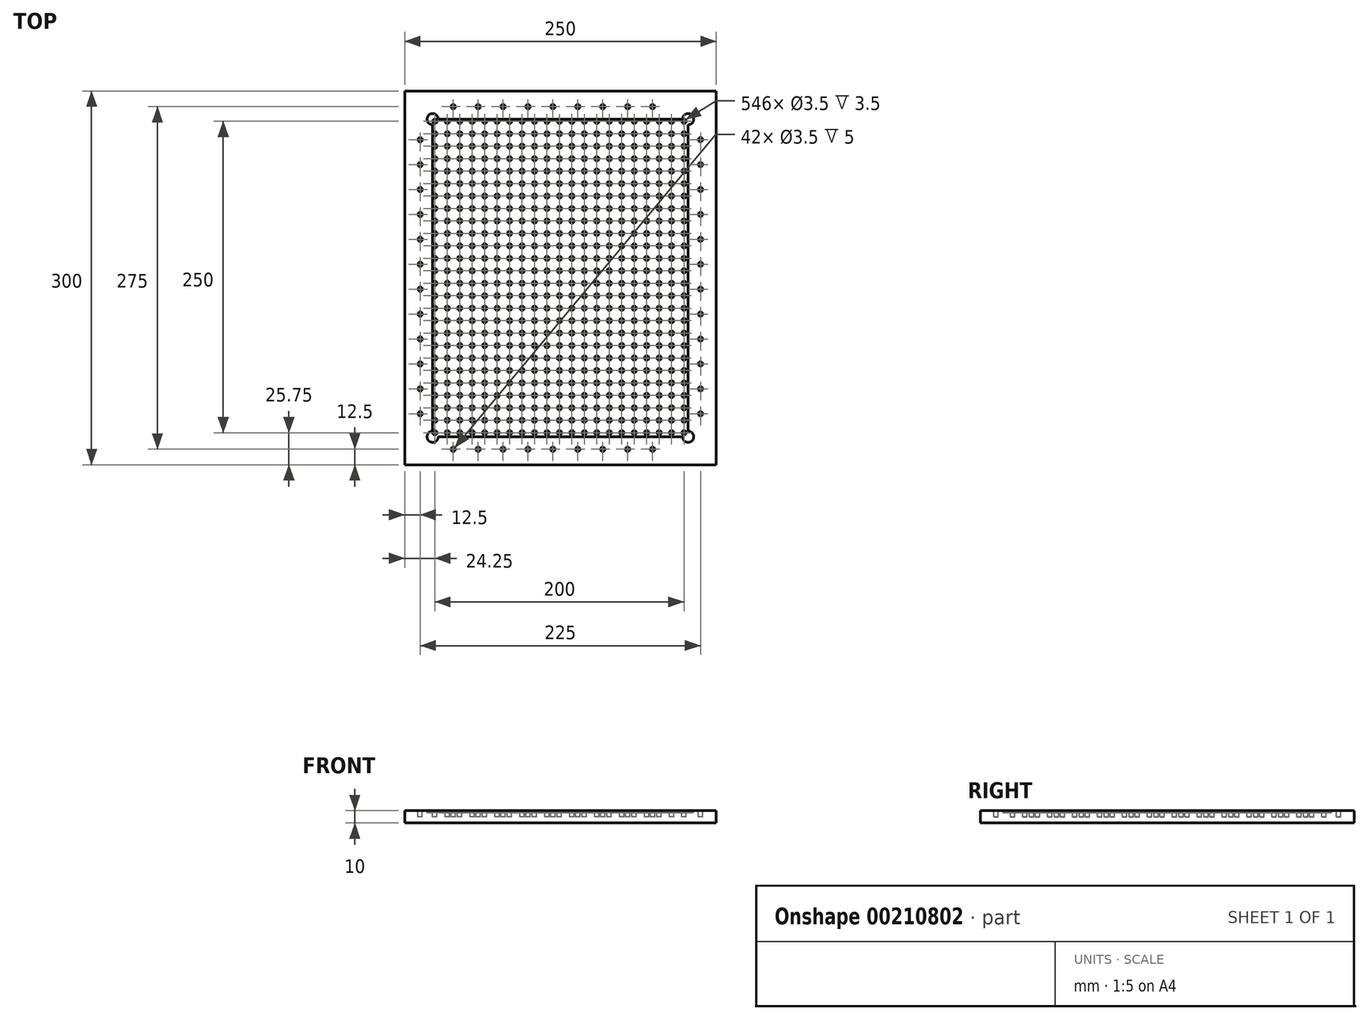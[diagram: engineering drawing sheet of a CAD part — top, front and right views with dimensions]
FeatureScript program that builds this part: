
annotation { "Feature Type Name" : "Feature", "Feature Type Description" : "" }
export const myFeature = defineFeature(function(context is Context, id is Id, definition is map)
    precondition{}
    {
        {
            var Q0;
            Q0=qCreatedBy(makeId("Top.planeOp"),FACE);
            var sketch = newSketch(context, id + "F0", { "sketchPlane" : qUnion([Q0])});
            skLineSegment(sketch, "E0.bottom", {"start": v(0, 0) * mm, "end": v(250, 0) * mm});
            skLineSegment(sketch, "E0.top", {"start": v(0, 300) * mm, "end": v(250, 300) * mm});
            skLineSegment(sketch, "E0.left", {"start": v(0, 0) * mm, "end": v(0, 300) * mm});
            skLineSegment(sketch, "E0.right", {"start": v(250, 0) * mm, "end": v(250, 300) * mm});
            skSolve(sketch);
        }
        {
            var Q0;
            Q0 = qSketchRegion(id + "F0", true);
            extrude(context, id + "F1", {"entities" : qUnion([Q0]), "depth" : 10 * mm});
        }
        {
            var Q0;
            Q0=makeQuery(id+"F1.opExtrude","CAP_FACE",FACE,{"disambiguationData":[OSD([sQuery(id+"F0.wireOp",EDGE,"E0.bottom"),sQuery(id+"F0.wireOp",EDGE,"E0.top"),sQuery(id+"F0.wireOp",EDGE,"E0.left"),sQuery(id+"F0.wireOp",EDGE,"E0.right")])],"isStart":false});
            var sketch = newSketch(context, id + "F2", { "sketchPlane" : qUnion([Q0])});
            skLineSegment(sketch, "E1.0", {"start": v(22.5, 277.5) * mm, "end": v(227.5, 277.5) * mm});
            skLineSegment(sketch, "E1.1", {"start": v(22.5, 22.5) * mm, "end": v(22.5, 277.5) * mm});
            skLineSegment(sketch, "E1.2", {"start": v(22.5, 22.5) * mm, "end": v(227.5, 22.5) * mm});
            skLineSegment(sketch, "E1.3", {"start": v(227.5, 22.5) * mm, "end": v(227.5, 277.5) * mm});
            skCircle(sketch, "E2", {"center": v(22.5, 277.5) * mm, "radius": 4.5 * mm});
            skCircle(sketch, "E3.0.1.0", {"center": v(22.5, 22.5) * mm, "radius": 4.5 * mm});
            skCircle(sketch, "E3.1.0.0", {"center": v(227.5, 277.5) * mm, "radius": 4.5 * mm});
            skCircle(sketch, "E3.1.1.0", {"center": v(227.5, 22.5) * mm, "radius": 4.5 * mm});
            skLineSegment(sketch, "E3.direction1", {"start": v(22.5, 277.5) * mm, "end": v(227.5, 277.5) * mm, "construction": true});
            skLineSegment(sketch, "E3.direction2", {"start": v(22.5, 277.5) * mm, "end": v(22.5, 22.5) * mm, "construction": true});
            skSolve(sketch);
        }
        {
            var Q0;
            Q0=makeQuery(id+"F2.imprint","IMPRINT",FACE,{"disambiguationData":[TD([[makeQuery(id+"F2.imprint","IMPRINT",EDGE,{"derivedFrom":makeQuery(id+"F1.opExtrude","CAP_EDGE",EDGE,{"disambiguationData":[OSD([sQuery(id+"F0.wireOp",EDGE,"E0.bottom")])],"isStart":false})}),1.0]])]});
            var sketch = newSketch(context, id + "F3", { "sketchPlane" : qUnion([Q0])});
            skCircle(sketch, "E4", {"center": v(24.25, 275.75) * mm, "radius": 1.75 * mm});
            skCircle(sketch, "E5.0.1.0", {"center": v(24.25, 265.75) * mm, "radius": 1.75 * mm});
            skCircle(sketch, "E5.0.2.0", {"center": v(24.25, 255.75) * mm, "radius": 1.75 * mm});
            skCircle(sketch, "E5.0.3.0", {"center": v(24.25, 245.75) * mm, "radius": 1.75 * mm});
            skCircle(sketch, "E5.0.4.0", {"center": v(24.25, 235.75) * mm, "radius": 1.75 * mm});
            skCircle(sketch, "E5.0.5.0", {"center": v(24.25, 225.75) * mm, "radius": 1.75 * mm});
            skCircle(sketch, "E5.0.6.0", {"center": v(24.25, 215.75) * mm, "radius": 1.75 * mm});
            skCircle(sketch, "E5.0.7.0", {"center": v(24.25, 205.75) * mm, "radius": 1.75 * mm});
            skCircle(sketch, "E5.0.8.0", {"center": v(24.25, 195.75) * mm, "radius": 1.75 * mm});
            skCircle(sketch, "E5.0.9.0", {"center": v(24.25, 185.75) * mm, "radius": 1.75 * mm});
            skCircle(sketch, "E5.0.10.0", {"center": v(24.25, 175.75) * mm, "radius": 1.75 * mm});
            skCircle(sketch, "E5.0.11.0", {"center": v(24.25, 165.75) * mm, "radius": 1.75 * mm});
            skCircle(sketch, "E5.0.12.0", {"center": v(24.25, 155.75) * mm, "radius": 1.75 * mm});
            skCircle(sketch, "E5.0.13.0", {"center": v(24.25, 145.75) * mm, "radius": 1.75 * mm});
            skCircle(sketch, "E5.0.14.0", {"center": v(24.25, 135.75) * mm, "radius": 1.75 * mm});
            skCircle(sketch, "E5.0.15.0", {"center": v(24.25, 125.75) * mm, "radius": 1.75 * mm});
            skCircle(sketch, "E5.0.16.0", {"center": v(24.25, 115.75) * mm, "radius": 1.75 * mm});
            skCircle(sketch, "E5.0.17.0", {"center": v(24.25, 105.75) * mm, "radius": 1.75 * mm});
            skCircle(sketch, "E5.0.18.0", {"center": v(24.25, 95.75) * mm, "radius": 1.75 * mm});
            skCircle(sketch, "E5.0.19.0", {"center": v(24.25, 85.75) * mm, "radius": 1.75 * mm});
            skCircle(sketch, "E5.0.20.0", {"center": v(24.25, 75.75) * mm, "radius": 1.75 * mm});
            skCircle(sketch, "E5.0.21.0", {"center": v(24.25, 65.75) * mm, "radius": 1.75 * mm});
            skCircle(sketch, "E5.0.22.0", {"center": v(24.25, 55.75) * mm, "radius": 1.75 * mm});
            skCircle(sketch, "E5.0.23.0", {"center": v(24.25, 45.75) * mm, "radius": 1.75 * mm});
            skCircle(sketch, "E5.0.24.0", {"center": v(24.25, 35.75) * mm, "radius": 1.75 * mm});
            skCircle(sketch, "E5.0.25.0", {"center": v(24.25, 25.75) * mm, "radius": 1.75 * mm});
            skCircle(sketch, "E5.1.0.0", {"center": v(34.25, 275.75) * mm, "radius": 1.75 * mm});
            skCircle(sketch, "E5.1.1.0", {"center": v(34.25, 265.75) * mm, "radius": 1.75 * mm});
            skCircle(sketch, "E5.1.2.0", {"center": v(34.25, 255.75) * mm, "radius": 1.75 * mm});
            skCircle(sketch, "E5.1.3.0", {"center": v(34.25, 245.75) * mm, "radius": 1.75 * mm});
            skCircle(sketch, "E5.1.4.0", {"center": v(34.25, 235.75) * mm, "radius": 1.75 * mm});
            skCircle(sketch, "E5.1.5.0", {"center": v(34.25, 225.75) * mm, "radius": 1.75 * mm});
            skCircle(sketch, "E5.1.6.0", {"center": v(34.25, 215.75) * mm, "radius": 1.75 * mm});
            skCircle(sketch, "E5.1.7.0", {"center": v(34.25, 205.75) * mm, "radius": 1.75 * mm});
            skCircle(sketch, "E5.1.8.0", {"center": v(34.25, 195.75) * mm, "radius": 1.75 * mm});
            skCircle(sketch, "E5.1.9.0", {"center": v(34.25, 185.75) * mm, "radius": 1.75 * mm});
            skCircle(sketch, "E5.1.10.0", {"center": v(34.25, 175.75) * mm, "radius": 1.75 * mm});
            skCircle(sketch, "E5.1.11.0", {"center": v(34.25, 165.75) * mm, "radius": 1.75 * mm});
            skCircle(sketch, "E5.1.12.0", {"center": v(34.25, 155.75) * mm, "radius": 1.75 * mm});
            skCircle(sketch, "E5.1.13.0", {"center": v(34.25, 145.75) * mm, "radius": 1.75 * mm});
            skCircle(sketch, "E5.1.14.0", {"center": v(34.25, 135.75) * mm, "radius": 1.75 * mm});
            skCircle(sketch, "E5.1.15.0", {"center": v(34.25, 125.75) * mm, "radius": 1.75 * mm});
            skCircle(sketch, "E5.1.16.0", {"center": v(34.25, 115.75) * mm, "radius": 1.75 * mm});
            skCircle(sketch, "E5.1.17.0", {"center": v(34.25, 105.75) * mm, "radius": 1.75 * mm});
            skCircle(sketch, "E5.1.18.0", {"center": v(34.25, 95.75) * mm, "radius": 1.75 * mm});
            skCircle(sketch, "E5.1.19.0", {"center": v(34.25, 85.75) * mm, "radius": 1.75 * mm});
            skCircle(sketch, "E5.1.20.0", {"center": v(34.25, 75.75) * mm, "radius": 1.75 * mm});
            skCircle(sketch, "E5.1.21.0", {"center": v(34.25, 65.75) * mm, "radius": 1.75 * mm});
            skCircle(sketch, "E5.1.22.0", {"center": v(34.25, 55.75) * mm, "radius": 1.75 * mm});
            skCircle(sketch, "E5.1.23.0", {"center": v(34.25, 45.75) * mm, "radius": 1.75 * mm});
            skCircle(sketch, "E5.1.24.0", {"center": v(34.25, 35.75) * mm, "radius": 1.75 * mm});
            skCircle(sketch, "E5.1.25.0", {"center": v(34.25, 25.75) * mm, "radius": 1.75 * mm});
            skCircle(sketch, "E5.2.0.0", {"center": v(44.25, 275.75) * mm, "radius": 1.75 * mm});
            skCircle(sketch, "E5.2.1.0", {"center": v(44.25, 265.75) * mm, "radius": 1.75 * mm});
            skCircle(sketch, "E5.2.2.0", {"center": v(44.25, 255.75) * mm, "radius": 1.75 * mm});
            skCircle(sketch, "E5.2.3.0", {"center": v(44.25, 245.75) * mm, "radius": 1.75 * mm});
            skCircle(sketch, "E5.2.4.0", {"center": v(44.25, 235.75) * mm, "radius": 1.75 * mm});
            skCircle(sketch, "E5.2.5.0", {"center": v(44.25, 225.75) * mm, "radius": 1.75 * mm});
            skCircle(sketch, "E5.2.6.0", {"center": v(44.25, 215.75) * mm, "radius": 1.75 * mm});
            skCircle(sketch, "E5.2.7.0", {"center": v(44.25, 205.75) * mm, "radius": 1.75 * mm});
            skCircle(sketch, "E5.2.8.0", {"center": v(44.25, 195.75) * mm, "radius": 1.75 * mm});
            skCircle(sketch, "E5.2.9.0", {"center": v(44.25, 185.75) * mm, "radius": 1.75 * mm});
            skCircle(sketch, "E5.2.10.0", {"center": v(44.25, 175.75) * mm, "radius": 1.75 * mm});
            skCircle(sketch, "E5.2.11.0", {"center": v(44.25, 165.75) * mm, "radius": 1.75 * mm});
            skCircle(sketch, "E5.2.12.0", {"center": v(44.25, 155.75) * mm, "radius": 1.75 * mm});
            skCircle(sketch, "E5.2.13.0", {"center": v(44.25, 145.75) * mm, "radius": 1.75 * mm});
            skCircle(sketch, "E5.2.14.0", {"center": v(44.25, 135.75) * mm, "radius": 1.75 * mm});
            skCircle(sketch, "E5.2.15.0", {"center": v(44.25, 125.75) * mm, "radius": 1.75 * mm});
            skCircle(sketch, "E5.2.16.0", {"center": v(44.25, 115.75) * mm, "radius": 1.75 * mm});
            skCircle(sketch, "E5.2.17.0", {"center": v(44.25, 105.75) * mm, "radius": 1.75 * mm});
            skCircle(sketch, "E5.2.18.0", {"center": v(44.25, 95.75) * mm, "radius": 1.75 * mm});
            skCircle(sketch, "E5.2.19.0", {"center": v(44.25, 85.75) * mm, "radius": 1.75 * mm});
            skCircle(sketch, "E5.2.20.0", {"center": v(44.25, 75.75) * mm, "radius": 1.75 * mm});
            skCircle(sketch, "E5.2.21.0", {"center": v(44.25, 65.75) * mm, "radius": 1.75 * mm});
            skCircle(sketch, "E5.2.22.0", {"center": v(44.25, 55.75) * mm, "radius": 1.75 * mm});
            skCircle(sketch, "E5.2.23.0", {"center": v(44.25, 45.75) * mm, "radius": 1.75 * mm});
            skCircle(sketch, "E5.2.24.0", {"center": v(44.25, 35.75) * mm, "radius": 1.75 * mm});
            skCircle(sketch, "E5.2.25.0", {"center": v(44.25, 25.75) * mm, "radius": 1.75 * mm});
            skCircle(sketch, "E5.3.0.0", {"center": v(54.25, 275.75) * mm, "radius": 1.75 * mm});
            skCircle(sketch, "E5.3.1.0", {"center": v(54.25, 265.75) * mm, "radius": 1.75 * mm});
            skCircle(sketch, "E5.3.2.0", {"center": v(54.25, 255.75) * mm, "radius": 1.75 * mm});
            skCircle(sketch, "E5.3.3.0", {"center": v(54.25, 245.75) * mm, "radius": 1.75 * mm});
            skCircle(sketch, "E5.3.4.0", {"center": v(54.25, 235.75) * mm, "radius": 1.75 * mm});
            skCircle(sketch, "E5.3.5.0", {"center": v(54.25, 225.75) * mm, "radius": 1.75 * mm});
            skCircle(sketch, "E5.3.6.0", {"center": v(54.25, 215.75) * mm, "radius": 1.75 * mm});
            skCircle(sketch, "E5.3.7.0", {"center": v(54.25, 205.75) * mm, "radius": 1.75 * mm});
            skCircle(sketch, "E5.3.8.0", {"center": v(54.25, 195.75) * mm, "radius": 1.75 * mm});
            skCircle(sketch, "E5.3.9.0", {"center": v(54.25, 185.75) * mm, "radius": 1.75 * mm});
            skCircle(sketch, "E5.3.10.0", {"center": v(54.25, 175.75) * mm, "radius": 1.75 * mm});
            skCircle(sketch, "E5.3.11.0", {"center": v(54.25, 165.75) * mm, "radius": 1.75 * mm});
            skCircle(sketch, "E5.3.12.0", {"center": v(54.25, 155.75) * mm, "radius": 1.75 * mm});
            skCircle(sketch, "E5.3.13.0", {"center": v(54.25, 145.75) * mm, "radius": 1.75 * mm});
            skCircle(sketch, "E5.3.14.0", {"center": v(54.25, 135.75) * mm, "radius": 1.75 * mm});
            skCircle(sketch, "E5.3.15.0", {"center": v(54.25, 125.75) * mm, "radius": 1.75 * mm});
            skCircle(sketch, "E5.3.16.0", {"center": v(54.25, 115.75) * mm, "radius": 1.75 * mm});
            skCircle(sketch, "E5.3.17.0", {"center": v(54.25, 105.75) * mm, "radius": 1.75 * mm});
            skCircle(sketch, "E5.3.18.0", {"center": v(54.25, 95.75) * mm, "radius": 1.75 * mm});
            skCircle(sketch, "E5.3.19.0", {"center": v(54.25, 85.75) * mm, "radius": 1.75 * mm});
            skCircle(sketch, "E5.3.20.0", {"center": v(54.25, 75.75) * mm, "radius": 1.75 * mm});
            skCircle(sketch, "E5.3.21.0", {"center": v(54.25, 65.75) * mm, "radius": 1.75 * mm});
            skCircle(sketch, "E5.3.22.0", {"center": v(54.25, 55.75) * mm, "radius": 1.75 * mm});
            skCircle(sketch, "E5.3.23.0", {"center": v(54.25, 45.75) * mm, "radius": 1.75 * mm});
            skCircle(sketch, "E5.3.24.0", {"center": v(54.25, 35.75) * mm, "radius": 1.75 * mm});
            skCircle(sketch, "E5.3.25.0", {"center": v(54.25, 25.75) * mm, "radius": 1.75 * mm});
            skCircle(sketch, "E5.4.0.0", {"center": v(64.25, 275.75) * mm, "radius": 1.75 * mm});
            skCircle(sketch, "E5.4.1.0", {"center": v(64.25, 265.75) * mm, "radius": 1.75 * mm});
            skCircle(sketch, "E5.4.2.0", {"center": v(64.25, 255.75) * mm, "radius": 1.75 * mm});
            skCircle(sketch, "E5.4.3.0", {"center": v(64.25, 245.75) * mm, "radius": 1.75 * mm});
            skCircle(sketch, "E5.4.4.0", {"center": v(64.25, 235.75) * mm, "radius": 1.75 * mm});
            skCircle(sketch, "E5.4.5.0", {"center": v(64.25, 225.75) * mm, "radius": 1.75 * mm});
            skCircle(sketch, "E5.4.6.0", {"center": v(64.25, 215.75) * mm, "radius": 1.75 * mm});
            skCircle(sketch, "E5.4.7.0", {"center": v(64.25, 205.75) * mm, "radius": 1.75 * mm});
            skCircle(sketch, "E5.4.8.0", {"center": v(64.25, 195.75) * mm, "radius": 1.75 * mm});
            skCircle(sketch, "E5.4.9.0", {"center": v(64.25, 185.75) * mm, "radius": 1.75 * mm});
            skCircle(sketch, "E5.4.10.0", {"center": v(64.25, 175.75) * mm, "radius": 1.75 * mm});
            skCircle(sketch, "E5.4.11.0", {"center": v(64.25, 165.75) * mm, "radius": 1.75 * mm});
            skCircle(sketch, "E5.4.12.0", {"center": v(64.25, 155.75) * mm, "radius": 1.75 * mm});
            skCircle(sketch, "E5.4.13.0", {"center": v(64.25, 145.75) * mm, "radius": 1.75 * mm});
            skCircle(sketch, "E5.4.14.0", {"center": v(64.25, 135.75) * mm, "radius": 1.75 * mm});
            skCircle(sketch, "E5.4.15.0", {"center": v(64.25, 125.75) * mm, "radius": 1.75 * mm});
            skCircle(sketch, "E5.4.16.0", {"center": v(64.25, 115.75) * mm, "radius": 1.75 * mm});
            skCircle(sketch, "E5.4.17.0", {"center": v(64.25, 105.75) * mm, "radius": 1.75 * mm});
            skCircle(sketch, "E5.4.18.0", {"center": v(64.25, 95.75) * mm, "radius": 1.75 * mm});
            skCircle(sketch, "E5.4.19.0", {"center": v(64.25, 85.75) * mm, "radius": 1.75 * mm});
            skCircle(sketch, "E5.4.20.0", {"center": v(64.25, 75.75) * mm, "radius": 1.75 * mm});
            skCircle(sketch, "E5.4.21.0", {"center": v(64.25, 65.75) * mm, "radius": 1.75 * mm});
            skCircle(sketch, "E5.4.22.0", {"center": v(64.25, 55.75) * mm, "radius": 1.75 * mm});
            skCircle(sketch, "E5.4.23.0", {"center": v(64.25, 45.75) * mm, "radius": 1.75 * mm});
            skCircle(sketch, "E5.4.24.0", {"center": v(64.25, 35.75) * mm, "radius": 1.75 * mm});
            skCircle(sketch, "E5.4.25.0", {"center": v(64.25, 25.75) * mm, "radius": 1.75 * mm});
            skCircle(sketch, "E5.5.0.0", {"center": v(74.25, 275.75) * mm, "radius": 1.75 * mm});
            skCircle(sketch, "E5.5.1.0", {"center": v(74.25, 265.75) * mm, "radius": 1.75 * mm});
            skCircle(sketch, "E5.5.2.0", {"center": v(74.25, 255.75) * mm, "radius": 1.75 * mm});
            skCircle(sketch, "E5.5.3.0", {"center": v(74.25, 245.75) * mm, "radius": 1.75 * mm});
            skCircle(sketch, "E5.5.4.0", {"center": v(74.25, 235.75) * mm, "radius": 1.75 * mm});
            skCircle(sketch, "E5.5.5.0", {"center": v(74.25, 225.75) * mm, "radius": 1.75 * mm});
            skCircle(sketch, "E5.5.6.0", {"center": v(74.25, 215.75) * mm, "radius": 1.75 * mm});
            skCircle(sketch, "E5.5.7.0", {"center": v(74.25, 205.75) * mm, "radius": 1.75 * mm});
            skCircle(sketch, "E5.5.8.0", {"center": v(74.25, 195.75) * mm, "radius": 1.75 * mm});
            skCircle(sketch, "E5.5.9.0", {"center": v(74.25, 185.75) * mm, "radius": 1.75 * mm});
            skCircle(sketch, "E5.5.10.0", {"center": v(74.25, 175.75) * mm, "radius": 1.75 * mm});
            skCircle(sketch, "E5.5.11.0", {"center": v(74.25, 165.75) * mm, "radius": 1.75 * mm});
            skCircle(sketch, "E5.5.12.0", {"center": v(74.25, 155.75) * mm, "radius": 1.75 * mm});
            skCircle(sketch, "E5.5.13.0", {"center": v(74.25, 145.75) * mm, "radius": 1.75 * mm});
            skCircle(sketch, "E5.5.14.0", {"center": v(74.25, 135.75) * mm, "radius": 1.75 * mm});
            skCircle(sketch, "E5.5.15.0", {"center": v(74.25, 125.75) * mm, "radius": 1.75 * mm});
            skCircle(sketch, "E5.5.16.0", {"center": v(74.25, 115.75) * mm, "radius": 1.75 * mm});
            skCircle(sketch, "E5.5.17.0", {"center": v(74.25, 105.75) * mm, "radius": 1.75 * mm});
            skCircle(sketch, "E5.5.18.0", {"center": v(74.25, 95.75) * mm, "radius": 1.75 * mm});
            skCircle(sketch, "E5.5.19.0", {"center": v(74.25, 85.75) * mm, "radius": 1.75 * mm});
            skCircle(sketch, "E5.5.20.0", {"center": v(74.25, 75.75) * mm, "radius": 1.75 * mm});
            skCircle(sketch, "E5.5.21.0", {"center": v(74.25, 65.75) * mm, "radius": 1.75 * mm});
            skCircle(sketch, "E5.5.22.0", {"center": v(74.25, 55.75) * mm, "radius": 1.75 * mm});
            skCircle(sketch, "E5.5.23.0", {"center": v(74.25, 45.75) * mm, "radius": 1.75 * mm});
            skCircle(sketch, "E5.5.24.0", {"center": v(74.25, 35.75) * mm, "radius": 1.75 * mm});
            skCircle(sketch, "E5.5.25.0", {"center": v(74.25, 25.75) * mm, "radius": 1.75 * mm});
            skCircle(sketch, "E5.6.0.0", {"center": v(84.25, 275.75) * mm, "radius": 1.75 * mm});
            skCircle(sketch, "E5.6.1.0", {"center": v(84.25, 265.75) * mm, "radius": 1.75 * mm});
            skCircle(sketch, "E5.6.2.0", {"center": v(84.25, 255.75) * mm, "radius": 1.75 * mm});
            skCircle(sketch, "E5.6.3.0", {"center": v(84.25, 245.75) * mm, "radius": 1.75 * mm});
            skCircle(sketch, "E5.6.4.0", {"center": v(84.25, 235.75) * mm, "radius": 1.75 * mm});
            skCircle(sketch, "E5.6.5.0", {"center": v(84.25, 225.75) * mm, "radius": 1.75 * mm});
            skCircle(sketch, "E5.6.6.0", {"center": v(84.25, 215.75) * mm, "radius": 1.75 * mm});
            skCircle(sketch, "E5.6.7.0", {"center": v(84.25, 205.75) * mm, "radius": 1.75 * mm});
            skCircle(sketch, "E5.6.8.0", {"center": v(84.25, 195.75) * mm, "radius": 1.75 * mm});
            skCircle(sketch, "E5.6.9.0", {"center": v(84.25, 185.75) * mm, "radius": 1.75 * mm});
            skCircle(sketch, "E5.6.10.0", {"center": v(84.25, 175.75) * mm, "radius": 1.75 * mm});
            skCircle(sketch, "E5.6.11.0", {"center": v(84.25, 165.75) * mm, "radius": 1.75 * mm});
            skCircle(sketch, "E5.6.12.0", {"center": v(84.25, 155.75) * mm, "radius": 1.75 * mm});
            skCircle(sketch, "E5.6.13.0", {"center": v(84.25, 145.75) * mm, "radius": 1.75 * mm});
            skCircle(sketch, "E5.6.14.0", {"center": v(84.25, 135.75) * mm, "radius": 1.75 * mm});
            skCircle(sketch, "E5.6.15.0", {"center": v(84.25, 125.75) * mm, "radius": 1.75 * mm});
            skCircle(sketch, "E5.6.16.0", {"center": v(84.25, 115.75) * mm, "radius": 1.75 * mm});
            skCircle(sketch, "E5.6.17.0", {"center": v(84.25, 105.75) * mm, "radius": 1.75 * mm});
            skCircle(sketch, "E5.6.18.0", {"center": v(84.25, 95.75) * mm, "radius": 1.75 * mm});
            skCircle(sketch, "E5.6.19.0", {"center": v(84.25, 85.75) * mm, "radius": 1.75 * mm});
            skCircle(sketch, "E5.6.20.0", {"center": v(84.25, 75.75) * mm, "radius": 1.75 * mm});
            skCircle(sketch, "E5.6.21.0", {"center": v(84.25, 65.75) * mm, "radius": 1.75 * mm});
            skCircle(sketch, "E5.6.22.0", {"center": v(84.25, 55.75) * mm, "radius": 1.75 * mm});
            skCircle(sketch, "E5.6.23.0", {"center": v(84.25, 45.75) * mm, "radius": 1.75 * mm});
            skCircle(sketch, "E5.6.24.0", {"center": v(84.25, 35.75) * mm, "radius": 1.75 * mm});
            skCircle(sketch, "E5.6.25.0", {"center": v(84.25, 25.75) * mm, "radius": 1.75 * mm});
            skCircle(sketch, "E5.7.0.0", {"center": v(94.25, 275.75) * mm, "radius": 1.75 * mm});
            skCircle(sketch, "E5.7.1.0", {"center": v(94.25, 265.75) * mm, "radius": 1.75 * mm});
            skCircle(sketch, "E5.7.2.0", {"center": v(94.25, 255.75) * mm, "radius": 1.75 * mm});
            skCircle(sketch, "E5.7.3.0", {"center": v(94.25, 245.75) * mm, "radius": 1.75 * mm});
            skCircle(sketch, "E5.7.4.0", {"center": v(94.25, 235.75) * mm, "radius": 1.75 * mm});
            skCircle(sketch, "E5.7.5.0", {"center": v(94.25, 225.75) * mm, "radius": 1.75 * mm});
            skCircle(sketch, "E5.7.6.0", {"center": v(94.25, 215.75) * mm, "radius": 1.75 * mm});
            skCircle(sketch, "E5.7.7.0", {"center": v(94.25, 205.75) * mm, "radius": 1.75 * mm});
            skCircle(sketch, "E5.7.8.0", {"center": v(94.25, 195.75) * mm, "radius": 1.75 * mm});
            skCircle(sketch, "E5.7.9.0", {"center": v(94.25, 185.75) * mm, "radius": 1.75 * mm});
            skCircle(sketch, "E5.7.10.0", {"center": v(94.25, 175.75) * mm, "radius": 1.75 * mm});
            skCircle(sketch, "E5.7.11.0", {"center": v(94.25, 165.75) * mm, "radius": 1.75 * mm});
            skCircle(sketch, "E5.7.12.0", {"center": v(94.25, 155.75) * mm, "radius": 1.75 * mm});
            skCircle(sketch, "E5.7.13.0", {"center": v(94.25, 145.75) * mm, "radius": 1.75 * mm});
            skCircle(sketch, "E5.7.14.0", {"center": v(94.25, 135.75) * mm, "radius": 1.75 * mm});
            skCircle(sketch, "E5.7.15.0", {"center": v(94.25, 125.75) * mm, "radius": 1.75 * mm});
            skCircle(sketch, "E5.7.16.0", {"center": v(94.25, 115.75) * mm, "radius": 1.75 * mm});
            skCircle(sketch, "E5.7.17.0", {"center": v(94.25, 105.75) * mm, "radius": 1.75 * mm});
            skCircle(sketch, "E5.7.18.0", {"center": v(94.25, 95.75) * mm, "radius": 1.75 * mm});
            skCircle(sketch, "E5.7.19.0", {"center": v(94.25, 85.75) * mm, "radius": 1.75 * mm});
            skCircle(sketch, "E5.7.20.0", {"center": v(94.25, 75.75) * mm, "radius": 1.75 * mm});
            skCircle(sketch, "E5.7.21.0", {"center": v(94.25, 65.75) * mm, "radius": 1.75 * mm});
            skCircle(sketch, "E5.7.22.0", {"center": v(94.25, 55.75) * mm, "radius": 1.75 * mm});
            skCircle(sketch, "E5.7.23.0", {"center": v(94.25, 45.75) * mm, "radius": 1.75 * mm});
            skCircle(sketch, "E5.7.24.0", {"center": v(94.25, 35.75) * mm, "radius": 1.75 * mm});
            skCircle(sketch, "E5.7.25.0", {"center": v(94.25, 25.75) * mm, "radius": 1.75 * mm});
            skCircle(sketch, "E5.8.0.0", {"center": v(104.25, 275.75) * mm, "radius": 1.75 * mm});
            skCircle(sketch, "E5.8.1.0", {"center": v(104.25, 265.75) * mm, "radius": 1.75 * mm});
            skCircle(sketch, "E5.8.2.0", {"center": v(104.25, 255.75) * mm, "radius": 1.75 * mm});
            skCircle(sketch, "E5.8.3.0", {"center": v(104.25, 245.75) * mm, "radius": 1.75 * mm});
            skCircle(sketch, "E5.8.4.0", {"center": v(104.25, 235.75) * mm, "radius": 1.75 * mm});
            skCircle(sketch, "E5.8.5.0", {"center": v(104.25, 225.75) * mm, "radius": 1.75 * mm});
            skCircle(sketch, "E5.8.6.0", {"center": v(104.25, 215.75) * mm, "radius": 1.75 * mm});
            skCircle(sketch, "E5.8.7.0", {"center": v(104.25, 205.75) * mm, "radius": 1.75 * mm});
            skCircle(sketch, "E5.8.8.0", {"center": v(104.25, 195.75) * mm, "radius": 1.75 * mm});
            skCircle(sketch, "E5.8.9.0", {"center": v(104.25, 185.75) * mm, "radius": 1.75 * mm});
            skCircle(sketch, "E5.8.10.0", {"center": v(104.25, 175.75) * mm, "radius": 1.75 * mm});
            skCircle(sketch, "E5.8.11.0", {"center": v(104.25, 165.75) * mm, "radius": 1.75 * mm});
            skCircle(sketch, "E5.8.12.0", {"center": v(104.25, 155.75) * mm, "radius": 1.75 * mm});
            skCircle(sketch, "E5.8.13.0", {"center": v(104.25, 145.75) * mm, "radius": 1.75 * mm});
            skCircle(sketch, "E5.8.14.0", {"center": v(104.25, 135.75) * mm, "radius": 1.75 * mm});
            skCircle(sketch, "E5.8.15.0", {"center": v(104.25, 125.75) * mm, "radius": 1.75 * mm});
            skCircle(sketch, "E5.8.16.0", {"center": v(104.25, 115.75) * mm, "radius": 1.75 * mm});
            skCircle(sketch, "E5.8.17.0", {"center": v(104.25, 105.75) * mm, "radius": 1.75 * mm});
            skCircle(sketch, "E5.8.18.0", {"center": v(104.25, 95.75) * mm, "radius": 1.75 * mm});
            skCircle(sketch, "E5.8.19.0", {"center": v(104.25, 85.75) * mm, "radius": 1.75 * mm});
            skCircle(sketch, "E5.8.20.0", {"center": v(104.25, 75.75) * mm, "radius": 1.75 * mm});
            skCircle(sketch, "E5.8.21.0", {"center": v(104.25, 65.75) * mm, "radius": 1.75 * mm});
            skCircle(sketch, "E5.8.22.0", {"center": v(104.25, 55.75) * mm, "radius": 1.75 * mm});
            skCircle(sketch, "E5.8.23.0", {"center": v(104.25, 45.75) * mm, "radius": 1.75 * mm});
            skCircle(sketch, "E5.8.24.0", {"center": v(104.25, 35.75) * mm, "radius": 1.75 * mm});
            skCircle(sketch, "E5.8.25.0", {"center": v(104.25, 25.75) * mm, "radius": 1.75 * mm});
            skCircle(sketch, "E5.9.0.0", {"center": v(114.25, 275.75) * mm, "radius": 1.75 * mm});
            skCircle(sketch, "E5.9.1.0", {"center": v(114.25, 265.75) * mm, "radius": 1.75 * mm});
            skCircle(sketch, "E5.9.2.0", {"center": v(114.25, 255.75) * mm, "radius": 1.75 * mm});
            skCircle(sketch, "E5.9.3.0", {"center": v(114.25, 245.75) * mm, "radius": 1.75 * mm});
            skCircle(sketch, "E5.9.4.0", {"center": v(114.25, 235.75) * mm, "radius": 1.75 * mm});
            skCircle(sketch, "E5.9.5.0", {"center": v(114.25, 225.75) * mm, "radius": 1.75 * mm});
            skCircle(sketch, "E5.9.6.0", {"center": v(114.25, 215.75) * mm, "radius": 1.75 * mm});
            skCircle(sketch, "E5.9.7.0", {"center": v(114.25, 205.75) * mm, "radius": 1.75 * mm});
            skCircle(sketch, "E5.9.8.0", {"center": v(114.25, 195.75) * mm, "radius": 1.75 * mm});
            skCircle(sketch, "E5.9.9.0", {"center": v(114.25, 185.75) * mm, "radius": 1.75 * mm});
            skCircle(sketch, "E5.9.10.0", {"center": v(114.25, 175.75) * mm, "radius": 1.75 * mm});
            skCircle(sketch, "E5.9.11.0", {"center": v(114.25, 165.75) * mm, "radius": 1.75 * mm});
            skCircle(sketch, "E5.9.12.0", {"center": v(114.25, 155.75) * mm, "radius": 1.75 * mm});
            skCircle(sketch, "E5.9.13.0", {"center": v(114.25, 145.75) * mm, "radius": 1.75 * mm});
            skCircle(sketch, "E5.9.14.0", {"center": v(114.25, 135.75) * mm, "radius": 1.75 * mm});
            skCircle(sketch, "E5.9.15.0", {"center": v(114.25, 125.75) * mm, "radius": 1.75 * mm});
            skCircle(sketch, "E5.9.16.0", {"center": v(114.25, 115.75) * mm, "radius": 1.75 * mm});
            skCircle(sketch, "E5.9.17.0", {"center": v(114.25, 105.75) * mm, "radius": 1.75 * mm});
            skCircle(sketch, "E5.9.18.0", {"center": v(114.25, 95.75) * mm, "radius": 1.75 * mm});
            skCircle(sketch, "E5.9.19.0", {"center": v(114.25, 85.75) * mm, "radius": 1.75 * mm});
            skCircle(sketch, "E5.9.20.0", {"center": v(114.25, 75.75) * mm, "radius": 1.75 * mm});
            skCircle(sketch, "E5.9.21.0", {"center": v(114.25, 65.75) * mm, "radius": 1.75 * mm});
            skCircle(sketch, "E5.9.22.0", {"center": v(114.25, 55.75) * mm, "radius": 1.75 * mm});
            skCircle(sketch, "E5.9.23.0", {"center": v(114.25, 45.75) * mm, "radius": 1.75 * mm});
            skCircle(sketch, "E5.9.24.0", {"center": v(114.25, 35.75) * mm, "radius": 1.75 * mm});
            skCircle(sketch, "E5.9.25.0", {"center": v(114.25, 25.75) * mm, "radius": 1.75 * mm});
            skCircle(sketch, "E5.10.0.0", {"center": v(124.25, 275.75) * mm, "radius": 1.75 * mm});
            skCircle(sketch, "E5.10.1.0", {"center": v(124.25, 265.75) * mm, "radius": 1.75 * mm});
            skCircle(sketch, "E5.10.2.0", {"center": v(124.25, 255.75) * mm, "radius": 1.75 * mm});
            skCircle(sketch, "E5.10.3.0", {"center": v(124.25, 245.75) * mm, "radius": 1.75 * mm});
            skCircle(sketch, "E5.10.4.0", {"center": v(124.25, 235.75) * mm, "radius": 1.75 * mm});
            skCircle(sketch, "E5.10.5.0", {"center": v(124.25, 225.75) * mm, "radius": 1.75 * mm});
            skCircle(sketch, "E5.10.6.0", {"center": v(124.25, 215.75) * mm, "radius": 1.75 * mm});
            skCircle(sketch, "E5.10.7.0", {"center": v(124.25, 205.75) * mm, "radius": 1.75 * mm});
            skCircle(sketch, "E5.10.8.0", {"center": v(124.25, 195.75) * mm, "radius": 1.75 * mm});
            skCircle(sketch, "E5.10.9.0", {"center": v(124.25, 185.75) * mm, "radius": 1.75 * mm});
            skCircle(sketch, "E5.10.10.0", {"center": v(124.25, 175.75) * mm, "radius": 1.75 * mm});
            skCircle(sketch, "E5.10.11.0", {"center": v(124.25, 165.75) * mm, "radius": 1.75 * mm});
            skCircle(sketch, "E5.10.12.0", {"center": v(124.25, 155.75) * mm, "radius": 1.75 * mm});
            skCircle(sketch, "E5.10.13.0", {"center": v(124.25, 145.75) * mm, "radius": 1.75 * mm});
            skCircle(sketch, "E5.10.14.0", {"center": v(124.25, 135.75) * mm, "radius": 1.75 * mm});
            skCircle(sketch, "E5.10.15.0", {"center": v(124.25, 125.75) * mm, "radius": 1.75 * mm});
            skCircle(sketch, "E5.10.16.0", {"center": v(124.25, 115.75) * mm, "radius": 1.75 * mm});
            skCircle(sketch, "E5.10.17.0", {"center": v(124.25, 105.75) * mm, "radius": 1.75 * mm});
            skCircle(sketch, "E5.10.18.0", {"center": v(124.25, 95.75) * mm, "radius": 1.75 * mm});
            skCircle(sketch, "E5.10.19.0", {"center": v(124.25, 85.75) * mm, "radius": 1.75 * mm});
            skCircle(sketch, "E5.10.20.0", {"center": v(124.25, 75.75) * mm, "radius": 1.75 * mm});
            skCircle(sketch, "E5.10.21.0", {"center": v(124.25, 65.75) * mm, "radius": 1.75 * mm});
            skCircle(sketch, "E5.10.22.0", {"center": v(124.25, 55.75) * mm, "radius": 1.75 * mm});
            skCircle(sketch, "E5.10.23.0", {"center": v(124.25, 45.75) * mm, "radius": 1.75 * mm});
            skCircle(sketch, "E5.10.24.0", {"center": v(124.25, 35.75) * mm, "radius": 1.75 * mm});
            skCircle(sketch, "E5.10.25.0", {"center": v(124.25, 25.75) * mm, "radius": 1.75 * mm});
            skCircle(sketch, "E5.11.0.0", {"center": v(134.25, 275.75) * mm, "radius": 1.75 * mm});
            skCircle(sketch, "E5.11.1.0", {"center": v(134.25, 265.75) * mm, "radius": 1.75 * mm});
            skCircle(sketch, "E5.11.2.0", {"center": v(134.25, 255.75) * mm, "radius": 1.75 * mm});
            skCircle(sketch, "E5.11.3.0", {"center": v(134.25, 245.75) * mm, "radius": 1.75 * mm});
            skCircle(sketch, "E5.11.4.0", {"center": v(134.25, 235.75) * mm, "radius": 1.75 * mm});
            skCircle(sketch, "E5.11.5.0", {"center": v(134.25, 225.75) * mm, "radius": 1.75 * mm});
            skCircle(sketch, "E5.11.6.0", {"center": v(134.25, 215.75) * mm, "radius": 1.75 * mm});
            skCircle(sketch, "E5.11.7.0", {"center": v(134.25, 205.75) * mm, "radius": 1.75 * mm});
            skCircle(sketch, "E5.11.8.0", {"center": v(134.25, 195.75) * mm, "radius": 1.75 * mm});
            skCircle(sketch, "E5.11.9.0", {"center": v(134.25, 185.75) * mm, "radius": 1.75 * mm});
            skCircle(sketch, "E5.11.10.0", {"center": v(134.25, 175.75) * mm, "radius": 1.75 * mm});
            skCircle(sketch, "E5.11.11.0", {"center": v(134.25, 165.75) * mm, "radius": 1.75 * mm});
            skCircle(sketch, "E5.11.12.0", {"center": v(134.25, 155.75) * mm, "radius": 1.75 * mm});
            skCircle(sketch, "E5.11.13.0", {"center": v(134.25, 145.75) * mm, "radius": 1.75 * mm});
            skCircle(sketch, "E5.11.14.0", {"center": v(134.25, 135.75) * mm, "radius": 1.75 * mm});
            skCircle(sketch, "E5.11.15.0", {"center": v(134.25, 125.75) * mm, "radius": 1.75 * mm});
            skCircle(sketch, "E5.11.16.0", {"center": v(134.25, 115.75) * mm, "radius": 1.75 * mm});
            skCircle(sketch, "E5.11.17.0", {"center": v(134.25, 105.75) * mm, "radius": 1.75 * mm});
            skCircle(sketch, "E5.11.18.0", {"center": v(134.25, 95.75) * mm, "radius": 1.75 * mm});
            skCircle(sketch, "E5.11.19.0", {"center": v(134.25, 85.75) * mm, "radius": 1.75 * mm});
            skCircle(sketch, "E5.11.20.0", {"center": v(134.25, 75.75) * mm, "radius": 1.75 * mm});
            skCircle(sketch, "E5.11.21.0", {"center": v(134.25, 65.75) * mm, "radius": 1.75 * mm});
            skCircle(sketch, "E5.11.22.0", {"center": v(134.25, 55.75) * mm, "radius": 1.75 * mm});
            skCircle(sketch, "E5.11.23.0", {"center": v(134.25, 45.75) * mm, "radius": 1.75 * mm});
            skCircle(sketch, "E5.11.24.0", {"center": v(134.25, 35.75) * mm, "radius": 1.75 * mm});
            skCircle(sketch, "E5.11.25.0", {"center": v(134.25, 25.75) * mm, "radius": 1.75 * mm});
            skCircle(sketch, "E5.12.0.0", {"center": v(144.25, 275.75) * mm, "radius": 1.75 * mm});
            skCircle(sketch, "E5.12.1.0", {"center": v(144.25, 265.75) * mm, "radius": 1.75 * mm});
            skCircle(sketch, "E5.12.2.0", {"center": v(144.25, 255.75) * mm, "radius": 1.75 * mm});
            skCircle(sketch, "E5.12.3.0", {"center": v(144.25, 245.75) * mm, "radius": 1.75 * mm});
            skCircle(sketch, "E5.12.4.0", {"center": v(144.25, 235.75) * mm, "radius": 1.75 * mm});
            skCircle(sketch, "E5.12.5.0", {"center": v(144.25, 225.75) * mm, "radius": 1.75 * mm});
            skCircle(sketch, "E5.12.6.0", {"center": v(144.25, 215.75) * mm, "radius": 1.75 * mm});
            skCircle(sketch, "E5.12.7.0", {"center": v(144.25, 205.75) * mm, "radius": 1.75 * mm});
            skCircle(sketch, "E5.12.8.0", {"center": v(144.25, 195.75) * mm, "radius": 1.75 * mm});
            skCircle(sketch, "E5.12.9.0", {"center": v(144.25, 185.75) * mm, "radius": 1.75 * mm});
            skCircle(sketch, "E5.12.10.0", {"center": v(144.25, 175.75) * mm, "radius": 1.75 * mm});
            skCircle(sketch, "E5.12.11.0", {"center": v(144.25, 165.75) * mm, "radius": 1.75 * mm});
            skCircle(sketch, "E5.12.12.0", {"center": v(144.25, 155.75) * mm, "radius": 1.75 * mm});
            skCircle(sketch, "E5.12.13.0", {"center": v(144.25, 145.75) * mm, "radius": 1.75 * mm});
            skCircle(sketch, "E5.12.14.0", {"center": v(144.25, 135.75) * mm, "radius": 1.75 * mm});
            skCircle(sketch, "E5.12.15.0", {"center": v(144.25, 125.75) * mm, "radius": 1.75 * mm});
            skCircle(sketch, "E5.12.16.0", {"center": v(144.25, 115.75) * mm, "radius": 1.75 * mm});
            skCircle(sketch, "E5.12.17.0", {"center": v(144.25, 105.75) * mm, "radius": 1.75 * mm});
            skCircle(sketch, "E5.12.18.0", {"center": v(144.25, 95.75) * mm, "radius": 1.75 * mm});
            skCircle(sketch, "E5.12.19.0", {"center": v(144.25, 85.75) * mm, "radius": 1.75 * mm});
            skCircle(sketch, "E5.12.20.0", {"center": v(144.25, 75.75) * mm, "radius": 1.75 * mm});
            skCircle(sketch, "E5.12.21.0", {"center": v(144.25, 65.75) * mm, "radius": 1.75 * mm});
            skCircle(sketch, "E5.12.22.0", {"center": v(144.25, 55.75) * mm, "radius": 1.75 * mm});
            skCircle(sketch, "E5.12.23.0", {"center": v(144.25, 45.75) * mm, "radius": 1.75 * mm});
            skCircle(sketch, "E5.12.24.0", {"center": v(144.25, 35.75) * mm, "radius": 1.75 * mm});
            skCircle(sketch, "E5.12.25.0", {"center": v(144.25, 25.75) * mm, "radius": 1.75 * mm});
            skCircle(sketch, "E5.13.0.0", {"center": v(154.25, 275.75) * mm, "radius": 1.75 * mm});
            skCircle(sketch, "E5.13.1.0", {"center": v(154.25, 265.75) * mm, "radius": 1.75 * mm});
            skCircle(sketch, "E5.13.2.0", {"center": v(154.25, 255.75) * mm, "radius": 1.75 * mm});
            skCircle(sketch, "E5.13.3.0", {"center": v(154.25, 245.75) * mm, "radius": 1.75 * mm});
            skCircle(sketch, "E5.13.4.0", {"center": v(154.25, 235.75) * mm, "radius": 1.75 * mm});
            skCircle(sketch, "E5.13.5.0", {"center": v(154.25, 225.75) * mm, "radius": 1.75 * mm});
            skCircle(sketch, "E5.13.6.0", {"center": v(154.25, 215.75) * mm, "radius": 1.75 * mm});
            skCircle(sketch, "E5.13.7.0", {"center": v(154.25, 205.75) * mm, "radius": 1.75 * mm});
            skCircle(sketch, "E5.13.8.0", {"center": v(154.25, 195.75) * mm, "radius": 1.75 * mm});
            skCircle(sketch, "E5.13.9.0", {"center": v(154.25, 185.75) * mm, "radius": 1.75 * mm});
            skCircle(sketch, "E5.13.10.0", {"center": v(154.25, 175.75) * mm, "radius": 1.75 * mm});
            skCircle(sketch, "E5.13.11.0", {"center": v(154.25, 165.75) * mm, "radius": 1.75 * mm});
            skCircle(sketch, "E5.13.12.0", {"center": v(154.25, 155.75) * mm, "radius": 1.75 * mm});
            skCircle(sketch, "E5.13.13.0", {"center": v(154.25, 145.75) * mm, "radius": 1.75 * mm});
            skCircle(sketch, "E5.13.14.0", {"center": v(154.25, 135.75) * mm, "radius": 1.75 * mm});
            skCircle(sketch, "E5.13.15.0", {"center": v(154.25, 125.75) * mm, "radius": 1.75 * mm});
            skCircle(sketch, "E5.13.16.0", {"center": v(154.25, 115.75) * mm, "radius": 1.75 * mm});
            skCircle(sketch, "E5.13.17.0", {"center": v(154.25, 105.75) * mm, "radius": 1.75 * mm});
            skCircle(sketch, "E5.13.18.0", {"center": v(154.25, 95.75) * mm, "radius": 1.75 * mm});
            skCircle(sketch, "E5.13.19.0", {"center": v(154.25, 85.75) * mm, "radius": 1.75 * mm});
            skCircle(sketch, "E5.13.20.0", {"center": v(154.25, 75.75) * mm, "radius": 1.75 * mm});
            skCircle(sketch, "E5.13.21.0", {"center": v(154.25, 65.75) * mm, "radius": 1.75 * mm});
            skCircle(sketch, "E5.13.22.0", {"center": v(154.25, 55.75) * mm, "radius": 1.75 * mm});
            skCircle(sketch, "E5.13.23.0", {"center": v(154.25, 45.75) * mm, "radius": 1.75 * mm});
            skCircle(sketch, "E5.13.24.0", {"center": v(154.25, 35.75) * mm, "radius": 1.75 * mm});
            skCircle(sketch, "E5.13.25.0", {"center": v(154.25, 25.75) * mm, "radius": 1.75 * mm});
            skCircle(sketch, "E5.14.0.0", {"center": v(164.25, 275.75) * mm, "radius": 1.75 * mm});
            skCircle(sketch, "E5.14.1.0", {"center": v(164.25, 265.75) * mm, "radius": 1.75 * mm});
            skCircle(sketch, "E5.14.2.0", {"center": v(164.25, 255.75) * mm, "radius": 1.75 * mm});
            skCircle(sketch, "E5.14.3.0", {"center": v(164.25, 245.75) * mm, "radius": 1.75 * mm});
            skCircle(sketch, "E5.14.4.0", {"center": v(164.25, 235.75) * mm, "radius": 1.75 * mm});
            skCircle(sketch, "E5.14.5.0", {"center": v(164.25, 225.75) * mm, "radius": 1.75 * mm});
            skCircle(sketch, "E5.14.6.0", {"center": v(164.25, 215.75) * mm, "radius": 1.75 * mm});
            skCircle(sketch, "E5.14.7.0", {"center": v(164.25, 205.75) * mm, "radius": 1.75 * mm});
            skCircle(sketch, "E5.14.8.0", {"center": v(164.25, 195.75) * mm, "radius": 1.75 * mm});
            skCircle(sketch, "E5.14.9.0", {"center": v(164.25, 185.75) * mm, "radius": 1.75 * mm});
            skCircle(sketch, "E5.14.10.0", {"center": v(164.25, 175.75) * mm, "radius": 1.75 * mm});
            skCircle(sketch, "E5.14.11.0", {"center": v(164.25, 165.75) * mm, "radius": 1.75 * mm});
            skCircle(sketch, "E5.14.12.0", {"center": v(164.25, 155.75) * mm, "radius": 1.75 * mm});
            skCircle(sketch, "E5.14.13.0", {"center": v(164.25, 145.75) * mm, "radius": 1.75 * mm});
            skCircle(sketch, "E5.14.14.0", {"center": v(164.25, 135.75) * mm, "radius": 1.75 * mm});
            skCircle(sketch, "E5.14.15.0", {"center": v(164.25, 125.75) * mm, "radius": 1.75 * mm});
            skCircle(sketch, "E5.14.16.0", {"center": v(164.25, 115.75) * mm, "radius": 1.75 * mm});
            skCircle(sketch, "E5.14.17.0", {"center": v(164.25, 105.75) * mm, "radius": 1.75 * mm});
            skCircle(sketch, "E5.14.18.0", {"center": v(164.25, 95.75) * mm, "radius": 1.75 * mm});
            skCircle(sketch, "E5.14.19.0", {"center": v(164.25, 85.75) * mm, "radius": 1.75 * mm});
            skCircle(sketch, "E5.14.20.0", {"center": v(164.25, 75.75) * mm, "radius": 1.75 * mm});
            skCircle(sketch, "E5.14.21.0", {"center": v(164.25, 65.75) * mm, "radius": 1.75 * mm});
            skCircle(sketch, "E5.14.22.0", {"center": v(164.25, 55.75) * mm, "radius": 1.75 * mm});
            skCircle(sketch, "E5.14.23.0", {"center": v(164.25, 45.75) * mm, "radius": 1.75 * mm});
            skCircle(sketch, "E5.14.24.0", {"center": v(164.25, 35.75) * mm, "radius": 1.75 * mm});
            skCircle(sketch, "E5.14.25.0", {"center": v(164.25, 25.75) * mm, "radius": 1.75 * mm});
            skCircle(sketch, "E5.15.0.0", {"center": v(174.25, 275.75) * mm, "radius": 1.75 * mm});
            skCircle(sketch, "E5.15.1.0", {"center": v(174.25, 265.75) * mm, "radius": 1.75 * mm});
            skCircle(sketch, "E5.15.2.0", {"center": v(174.25, 255.75) * mm, "radius": 1.75 * mm});
            skCircle(sketch, "E5.15.3.0", {"center": v(174.25, 245.75) * mm, "radius": 1.75 * mm});
            skCircle(sketch, "E5.15.4.0", {"center": v(174.25, 235.75) * mm, "radius": 1.75 * mm});
            skCircle(sketch, "E5.15.5.0", {"center": v(174.25, 225.75) * mm, "radius": 1.75 * mm});
            skCircle(sketch, "E5.15.6.0", {"center": v(174.25, 215.75) * mm, "radius": 1.75 * mm});
            skCircle(sketch, "E5.15.7.0", {"center": v(174.25, 205.75) * mm, "radius": 1.75 * mm});
            skCircle(sketch, "E5.15.8.0", {"center": v(174.25, 195.75) * mm, "radius": 1.75 * mm});
            skCircle(sketch, "E5.15.9.0", {"center": v(174.25, 185.75) * mm, "radius": 1.75 * mm});
            skCircle(sketch, "E5.15.10.0", {"center": v(174.25, 175.75) * mm, "radius": 1.75 * mm});
            skCircle(sketch, "E5.15.11.0", {"center": v(174.25, 165.75) * mm, "radius": 1.75 * mm});
            skCircle(sketch, "E5.15.12.0", {"center": v(174.25, 155.75) * mm, "radius": 1.75 * mm});
            skCircle(sketch, "E5.15.13.0", {"center": v(174.25, 145.75) * mm, "radius": 1.75 * mm});
            skCircle(sketch, "E5.15.14.0", {"center": v(174.25, 135.75) * mm, "radius": 1.75 * mm});
            skCircle(sketch, "E5.15.15.0", {"center": v(174.25, 125.75) * mm, "radius": 1.75 * mm});
            skCircle(sketch, "E5.15.16.0", {"center": v(174.25, 115.75) * mm, "radius": 1.75 * mm});
            skCircle(sketch, "E5.15.17.0", {"center": v(174.25, 105.75) * mm, "radius": 1.75 * mm});
            skCircle(sketch, "E5.15.18.0", {"center": v(174.25, 95.75) * mm, "radius": 1.75 * mm});
            skCircle(sketch, "E5.15.19.0", {"center": v(174.25, 85.75) * mm, "radius": 1.75 * mm});
            skCircle(sketch, "E5.15.20.0", {"center": v(174.25, 75.75) * mm, "radius": 1.75 * mm});
            skCircle(sketch, "E5.15.21.0", {"center": v(174.25, 65.75) * mm, "radius": 1.75 * mm});
            skCircle(sketch, "E5.15.22.0", {"center": v(174.25, 55.75) * mm, "radius": 1.75 * mm});
            skCircle(sketch, "E5.15.23.0", {"center": v(174.25, 45.75) * mm, "radius": 1.75 * mm});
            skCircle(sketch, "E5.15.24.0", {"center": v(174.25, 35.75) * mm, "radius": 1.75 * mm});
            skCircle(sketch, "E5.15.25.0", {"center": v(174.25, 25.75) * mm, "radius": 1.75 * mm});
            skCircle(sketch, "E5.16.0.0", {"center": v(184.25, 275.75) * mm, "radius": 1.75 * mm});
            skCircle(sketch, "E5.16.1.0", {"center": v(184.25, 265.75) * mm, "radius": 1.75 * mm});
            skCircle(sketch, "E5.16.2.0", {"center": v(184.25, 255.75) * mm, "radius": 1.75 * mm});
            skCircle(sketch, "E5.16.3.0", {"center": v(184.25, 245.75) * mm, "radius": 1.75 * mm});
            skCircle(sketch, "E5.16.4.0", {"center": v(184.25, 235.75) * mm, "radius": 1.75 * mm});
            skCircle(sketch, "E5.16.5.0", {"center": v(184.25, 225.75) * mm, "radius": 1.75 * mm});
            skCircle(sketch, "E5.16.6.0", {"center": v(184.25, 215.75) * mm, "radius": 1.75 * mm});
            skCircle(sketch, "E5.16.7.0", {"center": v(184.25, 205.75) * mm, "radius": 1.75 * mm});
            skCircle(sketch, "E5.16.8.0", {"center": v(184.25, 195.75) * mm, "radius": 1.75 * mm});
            skCircle(sketch, "E5.16.9.0", {"center": v(184.25, 185.75) * mm, "radius": 1.75 * mm});
            skCircle(sketch, "E5.16.10.0", {"center": v(184.25, 175.75) * mm, "radius": 1.75 * mm});
            skCircle(sketch, "E5.16.11.0", {"center": v(184.25, 165.75) * mm, "radius": 1.75 * mm});
            skCircle(sketch, "E5.16.12.0", {"center": v(184.25, 155.75) * mm, "radius": 1.75 * mm});
            skCircle(sketch, "E5.16.13.0", {"center": v(184.25, 145.75) * mm, "radius": 1.75 * mm});
            skCircle(sketch, "E5.16.14.0", {"center": v(184.25, 135.75) * mm, "radius": 1.75 * mm});
            skCircle(sketch, "E5.16.15.0", {"center": v(184.25, 125.75) * mm, "radius": 1.75 * mm});
            skCircle(sketch, "E5.16.16.0", {"center": v(184.25, 115.75) * mm, "radius": 1.75 * mm});
            skCircle(sketch, "E5.16.17.0", {"center": v(184.25, 105.75) * mm, "radius": 1.75 * mm});
            skCircle(sketch, "E5.16.18.0", {"center": v(184.25, 95.75) * mm, "radius": 1.75 * mm});
            skCircle(sketch, "E5.16.19.0", {"center": v(184.25, 85.75) * mm, "radius": 1.75 * mm});
            skCircle(sketch, "E5.16.20.0", {"center": v(184.25, 75.75) * mm, "radius": 1.75 * mm});
            skCircle(sketch, "E5.16.21.0", {"center": v(184.25, 65.75) * mm, "radius": 1.75 * mm});
            skCircle(sketch, "E5.16.22.0", {"center": v(184.25, 55.75) * mm, "radius": 1.75 * mm});
            skCircle(sketch, "E5.16.23.0", {"center": v(184.25, 45.75) * mm, "radius": 1.75 * mm});
            skCircle(sketch, "E5.16.24.0", {"center": v(184.25, 35.75) * mm, "radius": 1.75 * mm});
            skCircle(sketch, "E5.16.25.0", {"center": v(184.25, 25.75) * mm, "radius": 1.75 * mm});
            skCircle(sketch, "E5.17.0.0", {"center": v(194.25, 275.75) * mm, "radius": 1.75 * mm});
            skCircle(sketch, "E5.17.1.0", {"center": v(194.25, 265.75) * mm, "radius": 1.75 * mm});
            skCircle(sketch, "E5.17.2.0", {"center": v(194.25, 255.75) * mm, "radius": 1.75 * mm});
            skCircle(sketch, "E5.17.3.0", {"center": v(194.25, 245.75) * mm, "radius": 1.75 * mm});
            skCircle(sketch, "E5.17.4.0", {"center": v(194.25, 235.75) * mm, "radius": 1.75 * mm});
            skCircle(sketch, "E5.17.5.0", {"center": v(194.25, 225.75) * mm, "radius": 1.75 * mm});
            skCircle(sketch, "E5.17.6.0", {"center": v(194.25, 215.75) * mm, "radius": 1.75 * mm});
            skCircle(sketch, "E5.17.7.0", {"center": v(194.25, 205.75) * mm, "radius": 1.75 * mm});
            skCircle(sketch, "E5.17.8.0", {"center": v(194.25, 195.75) * mm, "radius": 1.75 * mm});
            skCircle(sketch, "E5.17.9.0", {"center": v(194.25, 185.75) * mm, "radius": 1.75 * mm});
            skCircle(sketch, "E5.17.10.0", {"center": v(194.25, 175.75) * mm, "radius": 1.75 * mm});
            skCircle(sketch, "E5.17.11.0", {"center": v(194.25, 165.75) * mm, "radius": 1.75 * mm});
            skCircle(sketch, "E5.17.12.0", {"center": v(194.25, 155.75) * mm, "radius": 1.75 * mm});
            skCircle(sketch, "E5.17.13.0", {"center": v(194.25, 145.75) * mm, "radius": 1.75 * mm});
            skCircle(sketch, "E5.17.14.0", {"center": v(194.25, 135.75) * mm, "radius": 1.75 * mm});
            skCircle(sketch, "E5.17.15.0", {"center": v(194.25, 125.75) * mm, "radius": 1.75 * mm});
            skCircle(sketch, "E5.17.16.0", {"center": v(194.25, 115.75) * mm, "radius": 1.75 * mm});
            skCircle(sketch, "E5.17.17.0", {"center": v(194.25, 105.75) * mm, "radius": 1.75 * mm});
            skCircle(sketch, "E5.17.18.0", {"center": v(194.25, 95.75) * mm, "radius": 1.75 * mm});
            skCircle(sketch, "E5.17.19.0", {"center": v(194.25, 85.75) * mm, "radius": 1.75 * mm});
            skCircle(sketch, "E5.17.20.0", {"center": v(194.25, 75.75) * mm, "radius": 1.75 * mm});
            skCircle(sketch, "E5.17.21.0", {"center": v(194.25, 65.75) * mm, "radius": 1.75 * mm});
            skCircle(sketch, "E5.17.22.0", {"center": v(194.25, 55.75) * mm, "radius": 1.75 * mm});
            skCircle(sketch, "E5.17.23.0", {"center": v(194.25, 45.75) * mm, "radius": 1.75 * mm});
            skCircle(sketch, "E5.17.24.0", {"center": v(194.25, 35.75) * mm, "radius": 1.75 * mm});
            skCircle(sketch, "E5.17.25.0", {"center": v(194.25, 25.75) * mm, "radius": 1.75 * mm});
            skCircle(sketch, "E5.18.0.0", {"center": v(204.25, 275.75) * mm, "radius": 1.75 * mm});
            skCircle(sketch, "E5.18.1.0", {"center": v(204.25, 265.75) * mm, "radius": 1.75 * mm});
            skCircle(sketch, "E5.18.2.0", {"center": v(204.25, 255.75) * mm, "radius": 1.75 * mm});
            skCircle(sketch, "E5.18.3.0", {"center": v(204.25, 245.75) * mm, "radius": 1.75 * mm});
            skCircle(sketch, "E5.18.4.0", {"center": v(204.25, 235.75) * mm, "radius": 1.75 * mm});
            skCircle(sketch, "E5.18.5.0", {"center": v(204.25, 225.75) * mm, "radius": 1.75 * mm});
            skCircle(sketch, "E5.18.6.0", {"center": v(204.25, 215.75) * mm, "radius": 1.75 * mm});
            skCircle(sketch, "E5.18.7.0", {"center": v(204.25, 205.75) * mm, "radius": 1.75 * mm});
            skCircle(sketch, "E5.18.8.0", {"center": v(204.25, 195.75) * mm, "radius": 1.75 * mm});
            skCircle(sketch, "E5.18.9.0", {"center": v(204.25, 185.75) * mm, "radius": 1.75 * mm});
            skCircle(sketch, "E5.18.10.0", {"center": v(204.25, 175.75) * mm, "radius": 1.75 * mm});
            skCircle(sketch, "E5.18.11.0", {"center": v(204.25, 165.75) * mm, "radius": 1.75 * mm});
            skCircle(sketch, "E5.18.12.0", {"center": v(204.25, 155.75) * mm, "radius": 1.75 * mm});
            skCircle(sketch, "E5.18.13.0", {"center": v(204.25, 145.75) * mm, "radius": 1.75 * mm});
            skCircle(sketch, "E5.18.14.0", {"center": v(204.25, 135.75) * mm, "radius": 1.75 * mm});
            skCircle(sketch, "E5.18.15.0", {"center": v(204.25, 125.75) * mm, "radius": 1.75 * mm});
            skCircle(sketch, "E5.18.16.0", {"center": v(204.25, 115.75) * mm, "radius": 1.75 * mm});
            skCircle(sketch, "E5.18.17.0", {"center": v(204.25, 105.75) * mm, "radius": 1.75 * mm});
            skCircle(sketch, "E5.18.18.0", {"center": v(204.25, 95.75) * mm, "radius": 1.75 * mm});
            skCircle(sketch, "E5.18.19.0", {"center": v(204.25, 85.75) * mm, "radius": 1.75 * mm});
            skCircle(sketch, "E5.18.20.0", {"center": v(204.25, 75.75) * mm, "radius": 1.75 * mm});
            skCircle(sketch, "E5.18.21.0", {"center": v(204.25, 65.75) * mm, "radius": 1.75 * mm});
            skCircle(sketch, "E5.18.22.0", {"center": v(204.25, 55.75) * mm, "radius": 1.75 * mm});
            skCircle(sketch, "E5.18.23.0", {"center": v(204.25, 45.75) * mm, "radius": 1.75 * mm});
            skCircle(sketch, "E5.18.24.0", {"center": v(204.25, 35.75) * mm, "radius": 1.75 * mm});
            skCircle(sketch, "E5.18.25.0", {"center": v(204.25, 25.75) * mm, "radius": 1.75 * mm});
            skCircle(sketch, "E5.19.0.0", {"center": v(214.25, 275.75) * mm, "radius": 1.75 * mm});
            skCircle(sketch, "E5.19.1.0", {"center": v(214.25, 265.75) * mm, "radius": 1.75 * mm});
            skCircle(sketch, "E5.19.2.0", {"center": v(214.25, 255.75) * mm, "radius": 1.75 * mm});
            skCircle(sketch, "E5.19.3.0", {"center": v(214.25, 245.75) * mm, "radius": 1.75 * mm});
            skCircle(sketch, "E5.19.4.0", {"center": v(214.25, 235.75) * mm, "radius": 1.75 * mm});
            skCircle(sketch, "E5.19.5.0", {"center": v(214.25, 225.75) * mm, "radius": 1.75 * mm});
            skCircle(sketch, "E5.19.6.0", {"center": v(214.25, 215.75) * mm, "radius": 1.75 * mm});
            skCircle(sketch, "E5.19.7.0", {"center": v(214.25, 205.75) * mm, "radius": 1.75 * mm});
            skCircle(sketch, "E5.19.8.0", {"center": v(214.25, 195.75) * mm, "radius": 1.75 * mm});
            skCircle(sketch, "E5.19.9.0", {"center": v(214.25, 185.75) * mm, "radius": 1.75 * mm});
            skCircle(sketch, "E5.19.10.0", {"center": v(214.25, 175.75) * mm, "radius": 1.75 * mm});
            skCircle(sketch, "E5.19.11.0", {"center": v(214.25, 165.75) * mm, "radius": 1.75 * mm});
            skCircle(sketch, "E5.19.12.0", {"center": v(214.25, 155.75) * mm, "radius": 1.75 * mm});
            skCircle(sketch, "E5.19.13.0", {"center": v(214.25, 145.75) * mm, "radius": 1.75 * mm});
            skCircle(sketch, "E5.19.14.0", {"center": v(214.25, 135.75) * mm, "radius": 1.75 * mm});
            skCircle(sketch, "E5.19.15.0", {"center": v(214.25, 125.75) * mm, "radius": 1.75 * mm});
            skCircle(sketch, "E5.19.16.0", {"center": v(214.25, 115.75) * mm, "radius": 1.75 * mm});
            skCircle(sketch, "E5.19.17.0", {"center": v(214.25, 105.75) * mm, "radius": 1.75 * mm});
            skCircle(sketch, "E5.19.18.0", {"center": v(214.25, 95.75) * mm, "radius": 1.75 * mm});
            skCircle(sketch, "E5.19.19.0", {"center": v(214.25, 85.75) * mm, "radius": 1.75 * mm});
            skCircle(sketch, "E5.19.20.0", {"center": v(214.25, 75.75) * mm, "radius": 1.75 * mm});
            skCircle(sketch, "E5.19.21.0", {"center": v(214.25, 65.75) * mm, "radius": 1.75 * mm});
            skCircle(sketch, "E5.19.22.0", {"center": v(214.25, 55.75) * mm, "radius": 1.75 * mm});
            skCircle(sketch, "E5.19.23.0", {"center": v(214.25, 45.75) * mm, "radius": 1.75 * mm});
            skCircle(sketch, "E5.19.24.0", {"center": v(214.25, 35.75) * mm, "radius": 1.75 * mm});
            skCircle(sketch, "E5.19.25.0", {"center": v(214.25, 25.75) * mm, "radius": 1.75 * mm});
            skCircle(sketch, "E5.20.0.0", {"center": v(224.25, 275.75) * mm, "radius": 1.75 * mm});
            skCircle(sketch, "E5.20.1.0", {"center": v(224.25, 265.75) * mm, "radius": 1.75 * mm});
            skCircle(sketch, "E5.20.2.0", {"center": v(224.25, 255.75) * mm, "radius": 1.75 * mm});
            skCircle(sketch, "E5.20.3.0", {"center": v(224.25, 245.75) * mm, "radius": 1.75 * mm});
            skCircle(sketch, "E5.20.4.0", {"center": v(224.25, 235.75) * mm, "radius": 1.75 * mm});
            skCircle(sketch, "E5.20.5.0", {"center": v(224.25, 225.75) * mm, "radius": 1.75 * mm});
            skCircle(sketch, "E5.20.6.0", {"center": v(224.25, 215.75) * mm, "radius": 1.75 * mm});
            skCircle(sketch, "E5.20.7.0", {"center": v(224.25, 205.75) * mm, "radius": 1.75 * mm});
            skCircle(sketch, "E5.20.8.0", {"center": v(224.25, 195.75) * mm, "radius": 1.75 * mm});
            skCircle(sketch, "E5.20.9.0", {"center": v(224.25, 185.75) * mm, "radius": 1.75 * mm});
            skCircle(sketch, "E5.20.10.0", {"center": v(224.25, 175.75) * mm, "radius": 1.75 * mm});
            skCircle(sketch, "E5.20.11.0", {"center": v(224.25, 165.75) * mm, "radius": 1.75 * mm});
            skCircle(sketch, "E5.20.12.0", {"center": v(224.25, 155.75) * mm, "radius": 1.75 * mm});
            skCircle(sketch, "E5.20.13.0", {"center": v(224.25, 145.75) * mm, "radius": 1.75 * mm});
            skCircle(sketch, "E5.20.14.0", {"center": v(224.25, 135.75) * mm, "radius": 1.75 * mm});
            skCircle(sketch, "E5.20.15.0", {"center": v(224.25, 125.75) * mm, "radius": 1.75 * mm});
            skCircle(sketch, "E5.20.16.0", {"center": v(224.25, 115.75) * mm, "radius": 1.75 * mm});
            skCircle(sketch, "E5.20.17.0", {"center": v(224.25, 105.75) * mm, "radius": 1.75 * mm});
            skCircle(sketch, "E5.20.18.0", {"center": v(224.25, 95.75) * mm, "radius": 1.75 * mm});
            skCircle(sketch, "E5.20.19.0", {"center": v(224.25, 85.75) * mm, "radius": 1.75 * mm});
            skCircle(sketch, "E5.20.20.0", {"center": v(224.25, 75.75) * mm, "radius": 1.75 * mm});
            skCircle(sketch, "E5.20.21.0", {"center": v(224.25, 65.75) * mm, "radius": 1.75 * mm});
            skCircle(sketch, "E5.20.22.0", {"center": v(224.25, 55.75) * mm, "radius": 1.75 * mm});
            skCircle(sketch, "E5.20.23.0", {"center": v(224.25, 45.75) * mm, "radius": 1.75 * mm});
            skCircle(sketch, "E5.20.24.0", {"center": v(224.25, 35.75) * mm, "radius": 1.75 * mm});
            skCircle(sketch, "E5.20.25.0", {"center": v(224.25, 25.75) * mm, "radius": 1.75 * mm});
            skLineSegment(sketch, "E5.direction1", {"start": v(24.25, 275.75) * mm, "end": v(34.25, 275.75) * mm, "construction": true});
            skLineSegment(sketch, "E5.direction2", {"start": v(24.25, 275.75) * mm, "end": v(24.25, 265.75) * mm, "construction": true});
            skSolve(sketch);
        }
        {
            var Q0;
            Q0 = qSketchRegion(id + "F3", true);
            extrude(context, id + "F4", {"entities" : qUnion([Q0]), "operationType" : NewBodyOperationType.REMOVE, "oppositeDirection" : true, "depth" : 5 * mm});
        }
        {
            var Q0;
            Q0=makeQuery(id+"F2.imprint","IMPRINT",FACE,{"disambiguationData":[TD([[makeQuery(id+"F2.imprint","IMPRINT",EDGE,{"derivedFrom":makeQuery(id+"F1.opExtrude","CAP_EDGE",EDGE,{"disambiguationData":[OSD([sQuery(id+"F0.wireOp",EDGE,"E0.bottom")])],"isStart":false})}),1.0]])]});
            var sketch = newSketch(context, id + "F5", { "sketchPlane" : qUnion([Q0])});
            skCircle(sketch, "E6", {"center": v(39, 287.5) * mm, "radius": 1.75 * mm});
            skCircle(sketch, "E7.0.1.0", {"center": v(39, 12.5) * mm, "radius": 1.75 * mm});
            skCircle(sketch, "E7.1.0.0", {"center": v(59, 287.5) * mm, "radius": 1.75 * mm});
            skCircle(sketch, "E7.1.1.0", {"center": v(59, 12.5) * mm, "radius": 1.75 * mm});
            skCircle(sketch, "E7.2.0.0", {"center": v(79, 287.5) * mm, "radius": 1.75 * mm});
            skCircle(sketch, "E7.2.1.0", {"center": v(79, 12.5) * mm, "radius": 1.75 * mm});
            skCircle(sketch, "E7.3.0.0", {"center": v(99, 287.5) * mm, "radius": 1.75 * mm});
            skCircle(sketch, "E7.3.1.0", {"center": v(99, 12.5) * mm, "radius": 1.75 * mm});
            skCircle(sketch, "E7.4.0.0", {"center": v(119, 287.5) * mm, "radius": 1.75 * mm});
            skCircle(sketch, "E7.4.1.0", {"center": v(119, 12.5) * mm, "radius": 1.75 * mm});
            skCircle(sketch, "E7.5.0.0", {"center": v(139, 287.5) * mm, "radius": 1.75 * mm});
            skCircle(sketch, "E7.5.1.0", {"center": v(139, 12.5) * mm, "radius": 1.75 * mm});
            skCircle(sketch, "E7.6.0.0", {"center": v(159, 287.5) * mm, "radius": 1.75 * mm});
            skCircle(sketch, "E7.6.1.0", {"center": v(159, 12.5) * mm, "radius": 1.75 * mm});
            skCircle(sketch, "E7.7.0.0", {"center": v(179, 287.5) * mm, "radius": 1.75 * mm});
            skCircle(sketch, "E7.7.1.0", {"center": v(179, 12.5) * mm, "radius": 1.75 * mm});
            skCircle(sketch, "E7.8.0.0", {"center": v(199, 287.5) * mm, "radius": 1.75 * mm});
            skCircle(sketch, "E7.8.1.0", {"center": v(199, 12.5) * mm, "radius": 1.75 * mm});
            skLineSegment(sketch, "E7.direction1", {"start": v(39, 287.5) * mm, "end": v(59, 287.5) * mm, "construction": true});
            skLineSegment(sketch, "E7.direction2", {"start": v(39, 287.5) * mm, "end": v(39, 12.5) * mm, "construction": true});
            skCircle(sketch, "E8", {"center": v(12.5, 261) * mm, "radius": 1.75 * mm});
            skCircle(sketch, "E9.0.1.0", {"center": v(12.5, 241) * mm, "radius": 1.75 * mm});
            skCircle(sketch, "E9.0.2.0", {"center": v(12.5, 221) * mm, "radius": 1.75 * mm});
            skCircle(sketch, "E9.0.3.0", {"center": v(12.5, 201) * mm, "radius": 1.75 * mm});
            skCircle(sketch, "E9.0.4.0", {"center": v(12.5, 181) * mm, "radius": 1.75 * mm});
            skCircle(sketch, "E9.0.5.0", {"center": v(12.5, 161) * mm, "radius": 1.75 * mm});
            skCircle(sketch, "E9.0.6.0", {"center": v(12.5, 141) * mm, "radius": 1.75 * mm});
            skCircle(sketch, "E9.0.7.0", {"center": v(12.5, 121) * mm, "radius": 1.75 * mm});
            skCircle(sketch, "E9.0.8.0", {"center": v(12.5, 101) * mm, "radius": 1.75 * mm});
            skCircle(sketch, "E9.0.9.0", {"center": v(12.5, 81) * mm, "radius": 1.75 * mm});
            skCircle(sketch, "E9.0.10.0", {"center": v(12.5, 61) * mm, "radius": 1.75 * mm});
            skCircle(sketch, "E9.0.11.0", {"center": v(12.5, 41) * mm, "radius": 1.75 * mm});
            skCircle(sketch, "E9.1.0.0", {"center": v(237.5, 261) * mm, "radius": 1.75 * mm});
            skCircle(sketch, "E9.1.1.0", {"center": v(237.5, 241) * mm, "radius": 1.75 * mm});
            skCircle(sketch, "E9.1.2.0", {"center": v(237.5, 221) * mm, "radius": 1.75 * mm});
            skCircle(sketch, "E9.1.3.0", {"center": v(237.5, 201) * mm, "radius": 1.75 * mm});
            skCircle(sketch, "E9.1.4.0", {"center": v(237.5, 181) * mm, "radius": 1.75 * mm});
            skCircle(sketch, "E9.1.5.0", {"center": v(237.5, 161) * mm, "radius": 1.75 * mm});
            skCircle(sketch, "E9.1.6.0", {"center": v(237.5, 141) * mm, "radius": 1.75 * mm});
            skCircle(sketch, "E9.1.7.0", {"center": v(237.5, 121) * mm, "radius": 1.75 * mm});
            skCircle(sketch, "E9.1.8.0", {"center": v(237.5, 101) * mm, "radius": 1.75 * mm});
            skCircle(sketch, "E9.1.9.0", {"center": v(237.5, 81) * mm, "radius": 1.75 * mm});
            skCircle(sketch, "E9.1.10.0", {"center": v(237.5, 61) * mm, "radius": 1.75 * mm});
            skCircle(sketch, "E9.1.11.0", {"center": v(237.5, 41) * mm, "radius": 1.75 * mm});
            skLineSegment(sketch, "E9.direction1", {"start": v(12.5, 261) * mm, "end": v(237.5, 261) * mm, "construction": true});
            skLineSegment(sketch, "E9.direction2", {"start": v(12.5, 261) * mm, "end": v(12.5, 241) * mm, "construction": true});
            skSolve(sketch);
        }
        {
            var Q0;
            Q0 = qSketchRegion(id + "F5", true);
            extrude(context, id + "F6", {"entities" : qUnion([Q0]), "operationType" : NewBodyOperationType.REMOVE, "oppositeDirection" : true, "depth" : 5 * mm});
        }
        {
            var Q0;
            Q0 = qSketchRegion(id + "F2", true);
            extrude(context, id + "F7", {"entities" : qUnion([Q0]), "operationType" : NewBodyOperationType.REMOVE, "oppositeDirection" : true, "depth" : 1.5 * mm});
        }
    });
